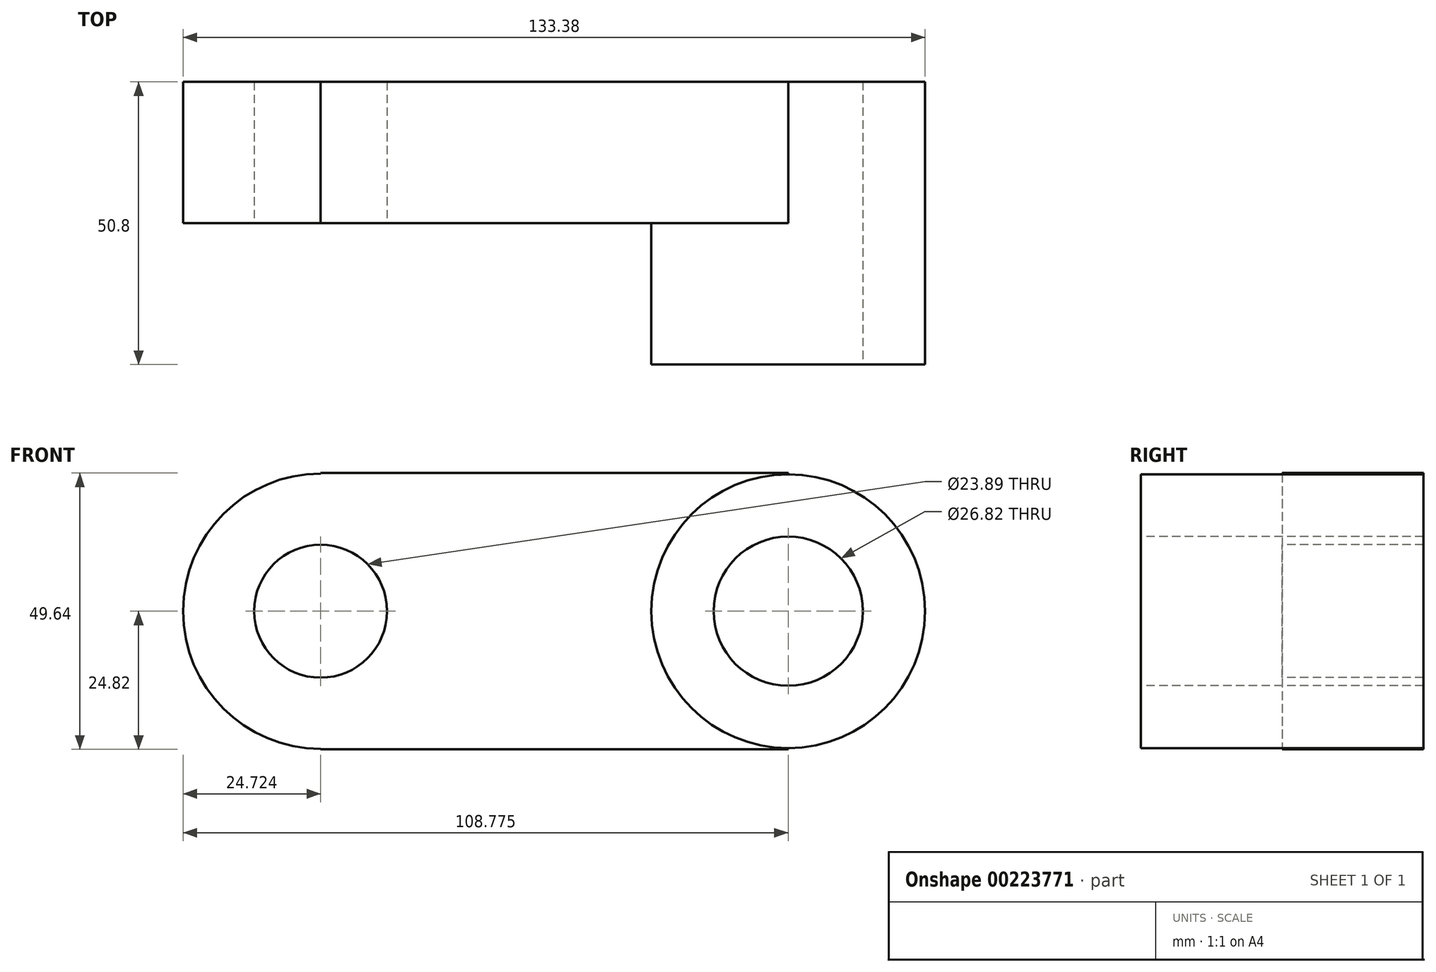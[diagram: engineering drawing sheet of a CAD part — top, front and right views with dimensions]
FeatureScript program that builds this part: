
annotation { "Feature Type Name" : "Feature", "Feature Type Description" : "" }
export const myFeature = defineFeature(function(context is Context, id is Id, definition is map)
    precondition{}
    {
        {
            var Q0;
            Q0=qCreatedBy(makeId("Front.planeOp"),FACE);
            var sketch = newSketch(context, id + "F0", { "sketchPlane" : qUnion([Q0])});
            skLineSegment(sketch, "E0.bottom", {"start": v(-42.03, 24.82) * mm, "end": v(42.03, 24.82) * mm});
            skLineSegment(sketch, "E0.top", {"start": v(-42.03, -24.82) * mm, "end": v(42.03, -24.82) * mm});
            skLineSegment(sketch, "E0.left", {"start": v(-42.03, 24.82) * mm, "end": v(-42.03, -24.82) * mm});
            skLineSegment(sketch, "E0.right", {"start": v(42.03, 24.82) * mm, "end": v(42.03, -24.82) * mm});
            skPoint(sketch, "E0.middle", {"position": v(0, 0) * mm});
            skSolve(sketch);
        }
        {
            var Q0;
            Q0=makeQuery(id+"F0.imprint","IMPRINT",FACE,{"disambiguationData":[TD([[makeQuery(id+"F0.imprint","IMPRINT",EDGE,{"derivedFrom":sQuery(id+"F0.wireOp",EDGE,"E0.bottom")}),-1.0]])]});
            var sketch = newSketch(context, id + "F1", { "sketchPlane" : qUnion([Q0])});
            skCircle(sketch, "E1", {"center": v(-42.03, 0) * mm, "radius": 24.72 * mm});
            skSolve(sketch);
        }
        {
            var Q0;
            Q0=makeQuery(id+"F0.imprint","IMPRINT",FACE,{"disambiguationData":[TD([[makeQuery(id+"F0.imprint","IMPRINT",EDGE,{"derivedFrom":sQuery(id+"F0.wireOp",EDGE,"E0.bottom")}),-1.0]])]});
            var sketch = newSketch(context, id + "F2", { "sketchPlane" : qUnion([Q0])});
            skCircle(sketch, "E2", {"center": v(42.03, 0) * mm, "radius": 24.6 * mm});
            skSolve(sketch);
        }
        {
            var Q0;
            {var subQ0=sQuery(id+"F2.wireOp",EDGE,"E2");var subQ1=makeQuery(id+"F0.imprint","IMPRINT",EDGE,{"derivedFrom":sQuery(id+"F0.wireOp",EDGE,"E0.right")});var subQ2=makeQuery(id+"F2.imprint","INTERSECT",VERTEX,{"disambiguationData":[OD(0.0)],"derivedFrom":[subQ1,subQ0]});Q0=makeQuery(id+"F2.imprint","IMPRINT",FACE,{"disambiguationData":[TD([[makeQuery(id+"F2.imprint","IMPRINT",EDGE,{"disambiguationData":[TD([[subQ2,1.0]])],"derivedFrom":subQ0}),1.0]])]});}
            var Q1;
            {var subQ0=sQuery(id+"F2.wireOp",EDGE,"E2");var subQ1=makeQuery(id+"F0.imprint","IMPRINT",EDGE,{"derivedFrom":sQuery(id+"F0.wireOp",EDGE,"E0.right")});var subQ2=makeQuery(id+"F2.imprint","INTERSECT",VERTEX,{"disambiguationData":[OD(0.0)],"derivedFrom":[subQ1,subQ0]});Q1=makeQuery(id+"F2.imprint","IMPRINT",FACE,{"disambiguationData":[TD([[makeQuery(id+"F2.imprint","IMPRINT",EDGE,{"disambiguationData":[TD([[subQ2,-1.0]])],"derivedFrom":subQ0}),1.0]])]});}
            extrude(context, id + "F3", {"entities" : qUnion([Q0, Q1]), "depth" : 50.8 * mm});
        }
        {
            var Q0;
            {var subQ1=makeQuery(id+"F0.imprint","IMPRINT",EDGE,{"derivedFrom":sQuery(id+"F0.wireOp",EDGE,"E0.bottom")});Q0=makeQuery(id+"F1.imprint","IMPRINT",FACE,{"disambiguationData":[TD([[makeQuery(id+"F1.imprint","IMPRINT",EDGE,{"derivedFrom":subQ1}),-1.0]])]});}
            var Q1;
            {var subQ0=sQuery(id+"F1.wireOp",EDGE,"E1");var subQ1=makeQuery(id+"F0.imprint","IMPRINT",EDGE,{"derivedFrom":sQuery(id+"F0.wireOp",EDGE,"E0.left")});var subQ2=makeQuery(id+"F1.imprint","INTERSECT",VERTEX,{"disambiguationData":[OD(0.0)],"derivedFrom":[subQ1,subQ0]});Q1=makeQuery(id+"F1.imprint","IMPRINT",FACE,{"disambiguationData":[TD([[makeQuery(id+"F1.imprint","IMPRINT",EDGE,{"disambiguationData":[TD([[subQ2,1.0]])],"derivedFrom":subQ0}),1.0]])]});}
            var Q2;
            {var subQ0=sQuery(id+"F1.wireOp",EDGE,"E1");var subQ1=makeQuery(id+"F0.imprint","IMPRINT",EDGE,{"derivedFrom":sQuery(id+"F0.wireOp",EDGE,"E0.left")});var subQ2=makeQuery(id+"F1.imprint","INTERSECT",VERTEX,{"disambiguationData":[OD(0.0)],"derivedFrom":[subQ1,subQ0]});Q2=makeQuery(id+"F1.imprint","IMPRINT",FACE,{"disambiguationData":[TD([[makeQuery(id+"F1.imprint","IMPRINT",EDGE,{"disambiguationData":[TD([[subQ2,-1.0]])],"derivedFrom":subQ0}),1.0]])]});}
            extrude(context, id + "F4", {"entities" : qUnion([Q0, Q1, Q2]), "operationType" : NewBodyOperationType.ADD, "depth" : 25.4 * mm});
        }
        {
            var Q0;
            Q0=makeQuery(id+"F4.opExtrude","CAP_FACE",FACE,{"disambiguationData":[OSD([sQuery(id+"F0.wireOp",EDGE,"E0.bottom"),sQuery(id+"F0.wireOp",EDGE,"E0.top"),sQuery(id+"F0.wireOp",EDGE,"E0.left"),sQuery(id+"F0.wireOp",EDGE,"E0.right"),sQuery(id+"F1.wireOp",EDGE,"E1")])],"isStart":false});
            var sketch = newSketch(context, id + "F5", { "sketchPlane" : qUnion([Q0])});
            skCircle(sketch, "E3", {"center": v(-42.03, 0) * mm, "radius": 11.95 * mm});
            skSolve(sketch);
        }
        {
            var Q0;
            Q0=makeQuery(id+"F5.imprint","IMPRINT",FACE,{"disambiguationData":[TD([[makeQuery(id+"F5.imprint","IMPRINT",EDGE,{"derivedFrom":sQuery(id+"F5.wireOp",EDGE,"E3")}),1.0]])]});
            extrude(context, id + "F6", {"entities" : qUnion([Q0]), "operationType" : NewBodyOperationType.REMOVE, "endBound" : BoundingType.THROUGH_ALL, "oppositeDirection" : true, "depth" : 25.4 * mm});
        }
        {
            var Q0;
            Q0=makeQuery(id+"F3.opExtrude","CAP_FACE",FACE,{"disambiguationData":[OSD([sQuery(id+"F2.wireOp",EDGE,"E2")])],"isStart":false});
            var sketch = newSketch(context, id + "F7", { "sketchPlane" : qUnion([Q0])});
            skCircle(sketch, "E4", {"center": v(42.03, 0) * mm, "radius": 13.41 * mm});
            skSolve(sketch);
        }
        {
            var Q0;
            Q0=makeQuery(id+"F7.imprint","IMPRINT",FACE,{"disambiguationData":[TD([[makeQuery(id+"F7.imprint","IMPRINT",EDGE,{"derivedFrom":sQuery(id+"F7.wireOp",EDGE,"E4")}),1.0]])]});
            extrude(context, id + "F8", {"entities" : qUnion([Q0]), "operationType" : NewBodyOperationType.REMOVE, "endBound" : BoundingType.THROUGH_ALL, "oppositeDirection" : true, "depth" : 25.4 * mm});
        }
    });
